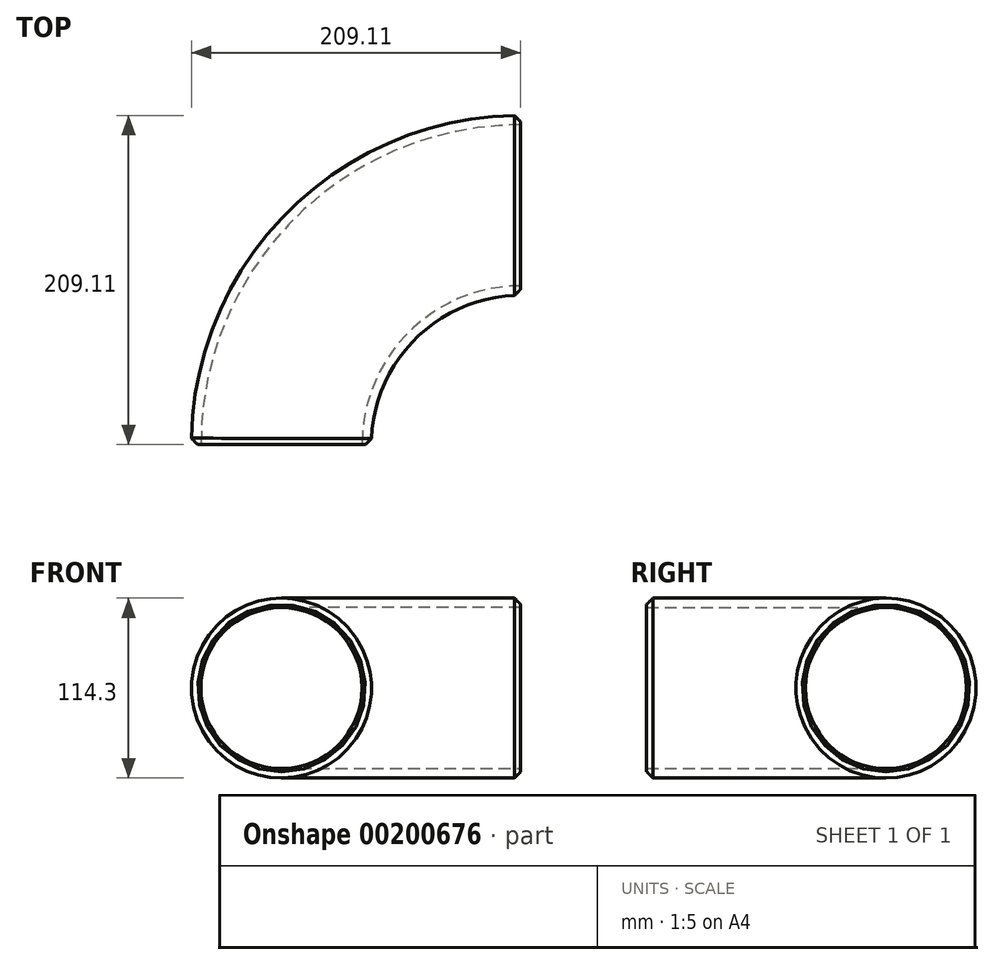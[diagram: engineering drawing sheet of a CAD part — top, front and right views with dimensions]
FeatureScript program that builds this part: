
annotation { "Feature Type Name" : "Feature", "Feature Type Description" : "" }
export const myFeature = defineFeature(function(context is Context, id is Id, definition is map)
    precondition{}
    {
        {
            assignVariable(context, id + "F0", {"name" : "B2", "anyValue" : 6});
        }
        {
            var Q0;
            Q0=qCreatedBy(makeId("Front.planeOp"),FACE);
            var sketch = newSketch(context, id + "F1", { "sketchPlane" : qUnion([Q0])});
            skCircle(sketch, "E0", {"center": v(0, 0) * mm, "radius": 57.15 * mm});
            skCircle(sketch, "E1", {"center": v(0, 0) * mm, "radius": 51.15 * mm});
            skSolve(sketch);
        }
        {
            var Q0;
            Q0=qCreatedBy(makeId("Top.planeOp"),FACE);
            var sketch = newSketch(context, id + "F2", { "sketchPlane" : qUnion([Q0])});
            skArc(sketch, "E2", {"start": v(0, 0) * mm, "mid": v(44.52, 107.48) * mm, "end": v(152, 152) * mm});
            skSolve(sketch);
        }
        {
            var Q0;
            Q0=makeQuery(id+"F1.imprint","IMPRINT",FACE,{"disambiguationData":[TD([[makeQuery(id+"F1.imprint","IMPRINT",EDGE,{"derivedFrom":sQuery(id+"F1.wireOp",EDGE,"E0")}),1.0]])]});
            var Q1;
            Q1=sQuery(id+"F2.wireOp",EDGE,"E2");
            sweep(context, id + "F3", {"profiles" : qUnion([Q0]), "path" : qUnion([Q1])});
        }
        {
            var Q0;
            Q0=makeQuery(id+"F3.opSweep","CAP_EDGE",EDGE,{"disambiguationData":[OSD([sQuery(id+"F1.wireOp",EDGE,"E0"),sQuery(id+"F2.wireOp",VERTEX,"E2.end")])],"isStart":false});
            var Q1;
            Q1=makeQuery(id+"F3.opSweep","CAP_EDGE",EDGE,{"disambiguationData":[OSD([sQuery(id+"F1.wireOp",EDGE,"E0"),sQuery(id+"F2.wireOp",VERTEX,"E2.start")])],"isStart":true});
            chamfer(context, id + "F4", {"entities" : qUnion([Q0, Q1]), "width" : (getVariable(context, 'B2') - 2) * mm, "tangentPropagation" : true});
        }
    });
